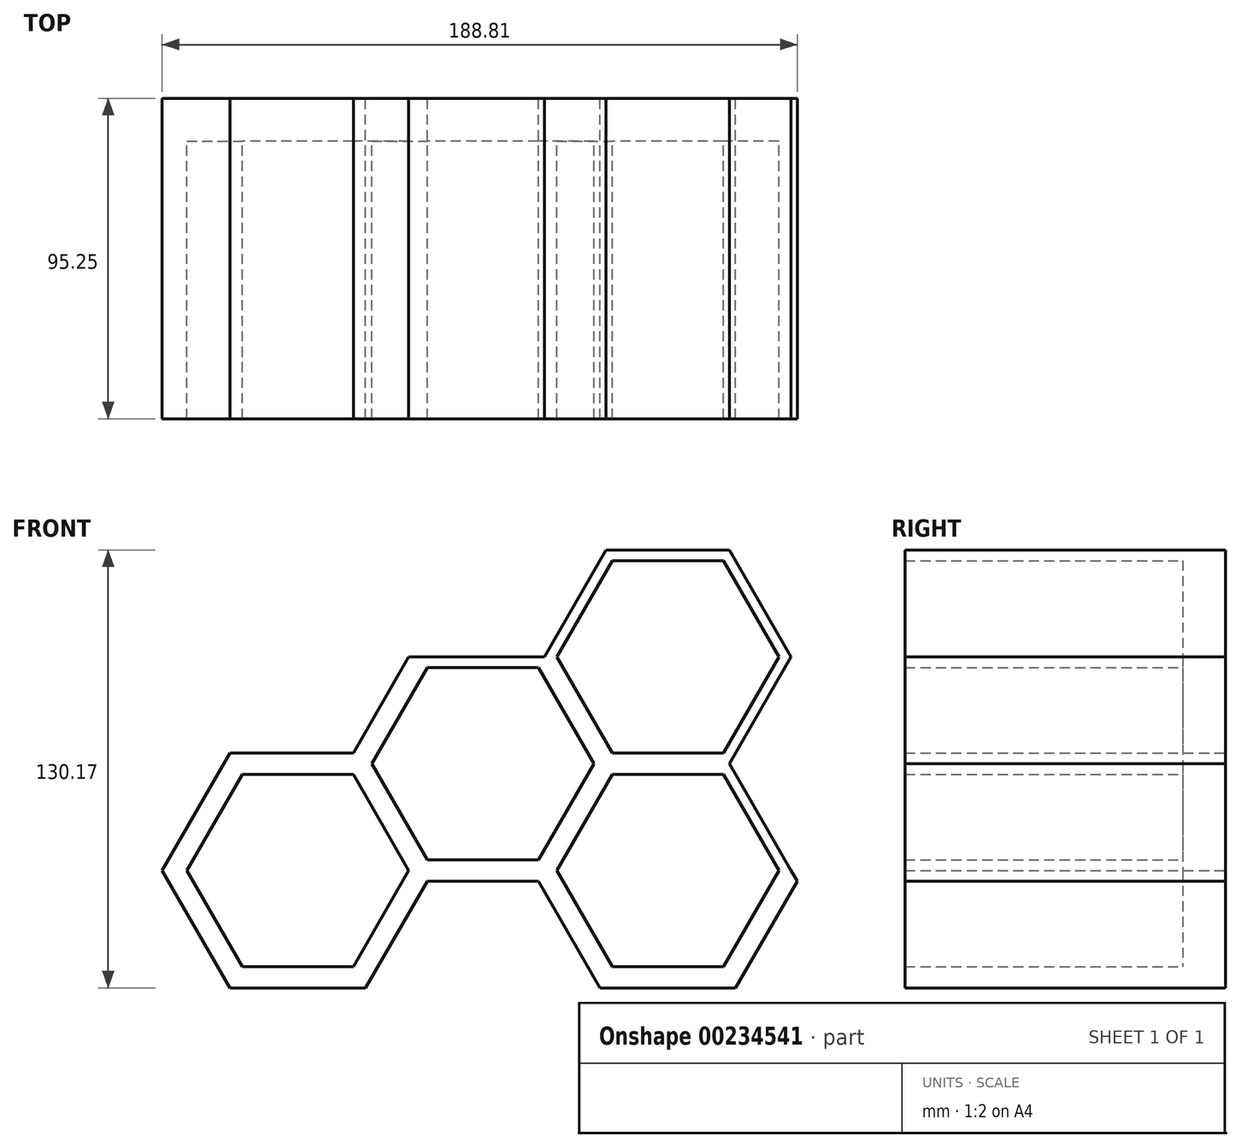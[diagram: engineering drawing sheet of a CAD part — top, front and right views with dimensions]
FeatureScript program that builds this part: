
annotation { "Feature Type Name" : "Feature", "Feature Type Description" : "" }
export const myFeature = defineFeature(function(context is Context, id is Id, definition is map)
    precondition{}
    {
        {
            var Q0;
            Q0=qCreatedBy(makeId("Front.planeOp"),FACE);
            var sketch = newSketch(context, id + "F0", { "sketchPlane" : qUnion([Q0])});
            skLineSegment(sketch, "E0.5", {"start": v(-59.27, 3.3) * mm, "end": v(-77.6, 35.04) * mm});
            skCircle(sketch, "E1.cCircle", {"center": v(-95.93, 3.3) * mm, "radius": 28.58 * mm, "construction": true});
            skLineSegment(sketch, "E1.0", {"start": v(-128.93, 3.3) * mm, "end": v(-112.43, 31.87) * mm});
            skLineSegment(sketch, "E1.1", {"start": v(-112.43, 31.87) * mm, "end": v(-79.43, 31.87) * mm});
            skLineSegment(sketch, "E1.2", {"start": v(-79.43, 31.87) * mm, "end": v(-62.94, 3.3) * mm});
            skLineSegment(sketch, "E1.3", {"start": v(-62.94, 3.3) * mm, "end": v(-79.43, -25.28) * mm});
            skLineSegment(sketch, "E1.4", {"start": v(-79.43, -25.28) * mm, "end": v(-112.43, -25.28) * mm});
            skLineSegment(sketch, "E1.5", {"start": v(-112.43, -25.28) * mm, "end": v(-128.93, 3.3) * mm});
            skPoint(sketch, "E1.0.midPoint", {"position": v(-120.68, 17.58) * mm});
            skCircle(sketch, "E2.cCircle", {"center": v(-95.93, 3.3) * mm, "radius": 31.75 * mm, "construction": true});
            skLineSegment(sketch, "E2.0", {"start": v(-132.6, 3.3) * mm, "end": v(-114.26, 35.04) * mm});
            skLineSegment(sketch, "E2.1", {"start": v(-114.26, 35.04) * mm, "end": v(-77.6, 35.04) * mm});
            skLineSegment(sketch, "E2.2", {"start": v(-77.6, 35.04) * mm, "end": v(-59.27, 3.3) * mm});
            skLineSegment(sketch, "E2.3", {"start": v(-59.27, 3.3) * mm, "end": v(-77.6, -28.46) * mm});
            skLineSegment(sketch, "E2.4", {"start": v(-77.6, -28.46) * mm, "end": v(-114.26, -28.46) * mm});
            skLineSegment(sketch, "E2.5", {"start": v(-114.26, -28.46) * mm, "end": v(-132.6, 3.3) * mm});
            skPoint(sketch, "E2.0.midPoint", {"position": v(-123.43, 19.17) * mm});
            skLineSegment(sketch, "E3.3", {"start": v(-114.26, 35.04) * mm, "end": v(-132.6, 3.3) * mm});
            skLineSegment(sketch, "E3.4", {"start": v(-132.6, 3.3) * mm, "end": v(-169.26, 3.3) * mm});
            skLineSegment(sketch, "E4.4", {"start": v(-77.6, 35.04) * mm, "end": v(-114.26, 35.04) * mm});
            skLineSegment(sketch, "E5.0", {"start": v(-77.6, -28.46) * mm, "end": v(-59.27, 3.3) * mm});
            skLineSegment(sketch, "E5.5", {"start": v(-59.27, -60.2) * mm, "end": v(-77.6, -28.46) * mm});
            skPoint(sketch, "E5.0.midPoint", {"position": v(-68.44, -12.58) * mm});
            skCircle(sketch, "E6.cCircle", {"center": v(-150.93, -28.46) * mm, "radius": 28.58 * mm, "construction": true});
            skLineSegment(sketch, "E6.0", {"start": v(-183.92, -28.46) * mm, "end": v(-167.42, 0.12) * mm});
            skLineSegment(sketch, "E6.1", {"start": v(-167.42, 0.12) * mm, "end": v(-134.43, 0.12) * mm});
            skLineSegment(sketch, "E6.2", {"start": v(-134.43, 0.12) * mm, "end": v(-117.93, -28.46) * mm});
            skLineSegment(sketch, "E6.3", {"start": v(-117.93, -28.46) * mm, "end": v(-134.43, -57.03) * mm});
            skLineSegment(sketch, "E6.4", {"start": v(-134.43, -57.03) * mm, "end": v(-167.42, -57.03) * mm});
            skLineSegment(sketch, "E6.5", {"start": v(-167.42, -57.03) * mm, "end": v(-183.92, -28.46) * mm});
            skPoint(sketch, "E6.0.midPoint", {"position": v(-175.67, -14.17) * mm});
            skCircle(sketch, "E7.cCircle", {"center": v(-150.93, -28.46) * mm, "radius": 31.75 * mm, "construction": true});
            skLineSegment(sketch, "E7.0", {"start": v(-187.59, -28.46) * mm, "end": v(-169.26, 3.3) * mm});
            skLineSegment(sketch, "E7.1", {"start": v(-169.26, 3.3) * mm, "end": v(-132.6, 3.3) * mm});
            skLineSegment(sketch, "E7.2", {"start": v(-132.6, 3.3) * mm, "end": v(-114.26, -28.46) * mm});
            skLineSegment(sketch, "E7.3", {"start": v(-114.26, -28.46) * mm, "end": v(-132.6, -60.2) * mm});
            skLineSegment(sketch, "E7.4", {"start": v(-132.6, -60.2) * mm, "end": v(-169.26, -60.2) * mm});
            skLineSegment(sketch, "E7.5", {"start": v(-169.26, -60.2) * mm, "end": v(-187.59, -28.46) * mm});
            skCircle(sketch, "E8.cCircle", {"center": v(-95.93, -60.2) * mm, "radius": 28.57 * mm, "construction": true});
            skLineSegment(sketch, "E8.0", {"start": v(-128.93, -60.2) * mm, "end": v(-112.43, -31.63) * mm});
            skLineSegment(sketch, "E8.1", {"start": v(-112.43, -31.63) * mm, "end": v(-79.43, -31.63) * mm});
            skLineSegment(sketch, "E8.2", {"start": v(-79.43, -31.63) * mm, "end": v(-62.94, -60.2) * mm});
            skLineSegment(sketch, "E8.3", {"start": v(-62.94, -60.2) * mm, "end": v(-79.43, -88.78) * mm});
            skLineSegment(sketch, "E8.4", {"start": v(-79.43, -88.78) * mm, "end": v(-112.43, -88.78) * mm});
            skLineSegment(sketch, "E8.5", {"start": v(-112.43, -88.78) * mm, "end": v(-128.93, -60.2) * mm});
            skPoint(sketch, "E8.0.midPoint", {"position": v(-120.68, -45.92) * mm});
            skCircle(sketch, "E9.cCircle", {"center": v(-95.93, -60.2) * mm, "radius": 31.75 * mm, "construction": true});
            skLineSegment(sketch, "E9.0", {"start": v(-132.6, -60.2) * mm, "end": v(-114.26, -28.46) * mm});
            skLineSegment(sketch, "E9.1", {"start": v(-114.26, -28.46) * mm, "end": v(-77.6, -28.46) * mm});
            skLineSegment(sketch, "E9.2", {"start": v(-77.6, -28.46) * mm, "end": v(-59.27, -60.2) * mm});
            skLineSegment(sketch, "E9.3", {"start": v(-59.27, -60.2) * mm, "end": v(-77.6, -91.96) * mm});
            skLineSegment(sketch, "E9.4", {"start": v(-77.6, -91.96) * mm, "end": v(-114.26, -91.96) * mm});
            skLineSegment(sketch, "E9.5", {"start": v(-114.26, -91.96) * mm, "end": v(-132.6, -60.2) * mm});
            skPoint(sketch, "E9.0.midPoint", {"position": v(-123.43, -44.33) * mm});
            skCircle(sketch, "E10.cCircle", {"center": v(-205.92, -60.2) * mm, "radius": 28.58 * mm, "construction": true});
            skLineSegment(sketch, "E10.0", {"start": v(-238.91, -60.2) * mm, "end": v(-222.42, -31.63) * mm});
            skLineSegment(sketch, "E10.1", {"start": v(-222.42, -31.63) * mm, "end": v(-189.42, -31.63) * mm});
            skLineSegment(sketch, "E10.2", {"start": v(-189.42, -31.63) * mm, "end": v(-172.92, -60.2) * mm});
            skLineSegment(sketch, "E10.3", {"start": v(-172.92, -60.2) * mm, "end": v(-189.42, -88.78) * mm});
            skLineSegment(sketch, "E10.4", {"start": v(-189.42, -88.78) * mm, "end": v(-222.42, -88.78) * mm});
            skLineSegment(sketch, "E10.5", {"start": v(-222.42, -88.78) * mm, "end": v(-238.91, -60.2) * mm});
            skPoint(sketch, "E10.0.midPoint", {"position": v(-230.66, -45.92) * mm});
            skCircle(sketch, "E11.cCircle", {"center": v(-205.92, -60.2) * mm, "radius": 31.75 * mm, "construction": true});
            skLineSegment(sketch, "E11.0", {"start": v(-242.58, -60.2) * mm, "end": v(-224.25, -28.46) * mm});
            skLineSegment(sketch, "E11.1", {"start": v(-224.25, -28.46) * mm, "end": v(-187.59, -28.46) * mm});
            skLineSegment(sketch, "E11.2", {"start": v(-187.59, -28.46) * mm, "end": v(-169.26, -60.2) * mm});
            skLineSegment(sketch, "E11.3", {"start": v(-169.26, -60.2) * mm, "end": v(-187.59, -91.96) * mm});
            skLineSegment(sketch, "E11.4", {"start": v(-187.59, -91.96) * mm, "end": v(-224.25, -91.96) * mm});
            skLineSegment(sketch, "E11.5", {"start": v(-224.25, -91.96) * mm, "end": v(-242.58, -60.2) * mm});
            skPoint(sketch, "E11.0.midPoint", {"position": v(-233.41, -44.33) * mm});
            skLineSegment(sketch, "E12", {"start": v(-172.92, 3.3) * mm, "end": v(-189.42, -25.28) * mm});
            skLineSegment(sketch, "E13", {"start": v(-189.42, -25.28) * mm, "end": v(-226.08, -25.28) * mm});
            skLineSegment(sketch, "E14", {"start": v(-226.08, -25.28) * mm, "end": v(-246.25, -60.2) * mm});
            skLineSegment(sketch, "E15", {"start": v(-246.25, -60.2) * mm, "end": v(-226.08, -95.13) * mm});
            skLineSegment(sketch, "E16", {"start": v(-226.08, -95.13) * mm, "end": v(-185.75, -95.13) * mm});
            skLineSegment(sketch, "E17", {"start": v(-185.75, -95.13) * mm, "end": v(-167.42, -63.38) * mm});
            skLineSegment(sketch, "E18", {"start": v(-167.42, -63.38) * mm, "end": v(-134.43, -63.38) * mm});
            skLineSegment(sketch, "E19", {"start": v(-134.43, -63.38) * mm, "end": v(-116.1, -95.13) * mm});
            skLineSegment(sketch, "E20", {"start": v(-116.1, -95.13) * mm, "end": v(-75.77, -95.13) * mm});
            skLineSegment(sketch, "E21", {"start": v(-75.77, -95.13) * mm, "end": v(-57.44, -63.38) * mm});
            skLineSegment(sketch, "E22", {"start": v(-172.92, 3.3) * mm, "end": v(-169.26, 3.3) * mm});
            skLineSegment(sketch, "E23", {"start": v(-57.44, -63.38) * mm, "end": v(-59.27, -60.2) * mm});
            skSolve(sketch);
        }
        {
            var Q0;
            Q0=makeQuery(id+"F0.imprint","IMPRINT",FACE,{"disambiguationData":[TD([[makeQuery(id+"F0.imprint","IMPRINT",EDGE,{"derivedFrom":sQuery(id+"F0.wireOp",EDGE,"68d16a58-0471-4e1c-b2b3-2a61df7c0d9d.0")}),-1.0]])]});
            var Q1;
            Q1=makeQuery(id+"F0.imprint","IMPRINT",FACE,{"disambiguationData":[TD([[makeQuery(id+"F0.imprint","IMPRINT",EDGE,{"derivedFrom":sQuery(id+"F0.wireOp",EDGE,"ae29455d-c252-400a-b569-c5a1c48e1351.0")}),-1.0]])]});
            var Q2;
            Q2=makeQuery(id+"F0.imprint","IMPRINT",FACE,{"disambiguationData":[TD([[makeQuery(id+"F0.imprint","IMPRINT",EDGE,{"derivedFrom":sQuery(id+"F0.wireOp",EDGE,"cad1e4f3-bd43-45ec-b31a-1d5006939c94.0")}),-1.0]])]});
            var Q3;
            Q3=makeQuery(id+"F0.imprint","IMPRINT",FACE,{"disambiguationData":[TD([[makeQuery(id+"F0.imprint","IMPRINT",EDGE,{"derivedFrom":sQuery(id+"F0.wireOp",EDGE,"E10.0")}),-1.0]])]});
            var Q4;
            Q4=makeQuery(id+"F0.imprint","IMPRINT",FACE,{"disambiguationData":[TD([[makeQuery(id+"F0.imprint","IMPRINT",EDGE,{"derivedFrom":sQuery(id+"F0.wireOp",EDGE,"8c75d941-d110-4871-aa41-90a72d60fb2b.0")}),-1.0]])]});
            var Q5;
            Q5=makeQuery(id+"F0.imprint","IMPRINT",FACE,{"disambiguationData":[TD([[makeQuery(id+"F0.imprint","IMPRINT",EDGE,{"derivedFrom":sQuery(id+"F0.wireOp",EDGE,"258573fa-3544-418e-8bc5-5d37e5b8ba09.0")}),-1.0]])]});
            var Q6;
            Q6=makeQuery(id+"F0.imprint","IMPRINT",FACE,{"disambiguationData":[TD([[makeQuery(id+"F0.imprint","IMPRINT",EDGE,{"derivedFrom":sQuery(id+"F0.wireOp",EDGE,"0bf0733b-7d93-4c2e-8366-56d2cde24658.0")}),-1.0]])]});
            var Q7;
            Q7=makeQuery(id+"F0.imprint","IMPRINT",FACE,{"disambiguationData":[TD([[makeQuery(id+"F0.imprint","IMPRINT",EDGE,{"derivedFrom":sQuery(id+"F0.wireOp",EDGE,"93717492-86db-456f-ae55-f71e4e93837b.0")}),-1.0]])]});
            var Q8;
            Q8=makeQuery(id+"F0.imprint","IMPRINT",FACE,{"disambiguationData":[TD([[makeQuery(id+"F0.imprint","IMPRINT",EDGE,{"derivedFrom":sQuery(id+"F0.wireOp",EDGE,"f16ea8c9-6b67-4651-8441-f7eb3c0ce7d7.0")}),-1.0]])]});
            var Q9;
            Q9=makeQuery(id+"F0.imprint","IMPRINT",FACE,{"disambiguationData":[TD([[makeQuery(id+"F0.imprint","IMPRINT",EDGE,{"derivedFrom":sQuery(id+"F0.wireOp",EDGE,"0306a0a6-7289-4661-a415-5fa5585f2cb5.0")}),-1.0]])]});
            var Q10;
            Q10=makeQuery(id+"F0.imprint","IMPRINT",FACE,{"disambiguationData":[TD([[makeQuery(id+"F0.imprint","IMPRINT",EDGE,{"derivedFrom":sQuery(id+"F0.wireOp",EDGE,"0a91a14e-ea0c-483f-91eb-c48bd73cb0e6.0")}),-1.0]])]});
            var Q11;
            Q11=makeQuery(id+"F0.imprint","IMPRINT",FACE,{"disambiguationData":[TD([[makeQuery(id+"F0.imprint","IMPRINT",EDGE,{"derivedFrom":sQuery(id+"F0.wireOp",EDGE,"E8.0")}),-1.0]])]});
            var Q12;
            Q12=makeQuery(id+"F0.imprint","IMPRINT",FACE,{"disambiguationData":[TD([[makeQuery(id+"F0.imprint","IMPRINT",EDGE,{"derivedFrom":sQuery(id+"F0.wireOp",EDGE,"E6.0")}),-1.0]])]});
            var Q13;
            Q13=makeQuery(id+"F0.imprint","IMPRINT",FACE,{"disambiguationData":[TD([[makeQuery(id+"F0.imprint","IMPRINT",EDGE,{"derivedFrom":sQuery(id+"F0.wireOp",EDGE,"084ca30c-4dc0-463f-bfd9-557787ed9a2f.0")}),-1.0]])]});
            var Q14;
            Q14=makeQuery(id+"F0.imprint","IMPRINT",FACE,{"disambiguationData":[TD([[makeQuery(id+"F0.imprint","IMPRINT",EDGE,{"derivedFrom":sQuery(id+"F0.wireOp",EDGE,"06c29831-6b25-410b-9247-4ee044b7735c.0")}),-1.0]])]});
            var Q15;
            Q15=makeQuery(id+"F0.imprint","IMPRINT",FACE,{"disambiguationData":[TD([[makeQuery(id+"F0.imprint","IMPRINT",EDGE,{"derivedFrom":sQuery(id+"F0.wireOp",EDGE,"b8eec94e-d97e-439b-aaac-63499233db4c.0")}),-1.0]])]});
            var Q16;
            Q16=makeQuery(id+"F0.imprint","IMPRINT",FACE,{"disambiguationData":[TD([[makeQuery(id+"F0.imprint","IMPRINT",EDGE,{"derivedFrom":sQuery(id+"F0.wireOp",EDGE,"2e929887-9bb9-4083-9cef-f9a6a24e8e46.0")}),-1.0]])]});
            var Q17;
            Q17=makeQuery(id+"F0.imprint","IMPRINT",FACE,{"disambiguationData":[TD([[makeQuery(id+"F0.imprint","IMPRINT",EDGE,{"derivedFrom":sQuery(id+"F0.wireOp",EDGE,"23671680-92ab-419e-a071-eb0943a5012b.0")}),-1.0]])]});
            var Q18;
            Q18=makeQuery(id+"F0.imprint","IMPRINT",FACE,{"disambiguationData":[TD([[makeQuery(id+"F0.imprint","IMPRINT",EDGE,{"derivedFrom":sQuery(id+"F0.wireOp",EDGE,"a1daa6ae-7864-4614-8fb9-3511dddc1266.0")}),-1.0]])]});
            var Q19;
            Q19=makeQuery(id+"F0.imprint","IMPRINT",FACE,{"disambiguationData":[TD([[makeQuery(id+"F0.imprint","IMPRINT",EDGE,{"derivedFrom":sQuery(id+"F0.wireOp",EDGE,"E1.0")}),-1.0]])]});
            var Q20;
            Q20=makeQuery(id+"F0.imprint","IMPRINT",FACE,{"disambiguationData":[TD([[makeQuery(id+"F0.imprint","IMPRINT",EDGE,{"derivedFrom":sQuery(id+"F0.wireOp",EDGE,"f2dd3995-374a-43c5-8725-4a87181dc8c5.0")}),-1.0]])]});
            var Q21;
            Q21=makeQuery(id+"F0.imprint","IMPRINT",FACE,{"disambiguationData":[TD([[makeQuery(id+"F0.imprint","IMPRINT",EDGE,{"derivedFrom":sQuery(id+"F0.wireOp",EDGE,"1f2aec04-a318-49b9-a42e-ea2fce35ed6c.0")}),-1.0]])]});
            var Q22;
            Q22=makeQuery(id+"F0.imprint","IMPRINT",FACE,{"disambiguationData":[TD([[makeQuery(id+"F0.imprint","IMPRINT",EDGE,{"derivedFrom":sQuery(id+"F0.wireOp",EDGE,"f97fdbdd-69fc-44f1-b8f7-f6a6a25558e6.0")}),-1.0]])]});
            var Q23;
            Q23=makeQuery(id+"F0.imprint","IMPRINT",FACE,{"disambiguationData":[TD([[makeQuery(id+"F0.imprint","IMPRINT",EDGE,{"derivedFrom":sQuery(id+"F0.wireOp",EDGE,"4e92e904-9607-490d-a429-b319c41500d9.0")}),-1.0]])]});
            var Q24;
            Q24=makeQuery(id+"F0.imprint","IMPRINT",FACE,{"disambiguationData":[TD([[makeQuery(id+"F0.imprint","IMPRINT",EDGE,{"derivedFrom":sQuery(id+"F0.wireOp",EDGE,"084ca30c-4dc0-463f-bfd9-557787ed9a2f.0")}),1.0]])]});
            var Q25;
            Q25=makeQuery(id+"F0.imprint","IMPRINT",FACE,{"disambiguationData":[TD([[makeQuery(id+"F0.imprint","IMPRINT",EDGE,{"derivedFrom":sQuery(id+"F0.wireOp",EDGE,"1f2aec04-a318-49b9-a42e-ea2fce35ed6c.0")}),1.0]])]});
            var Q26;
            Q26=makeQuery(id+"F0.imprint","IMPRINT",FACE,{"disambiguationData":[TD([[makeQuery(id+"F0.imprint","IMPRINT",EDGE,{"derivedFrom":sQuery(id+"F0.wireOp",EDGE,"23671680-92ab-419e-a071-eb0943a5012b.0")}),1.0]])]});
            var Q27;
            Q27=makeQuery(id+"F0.imprint","IMPRINT",FACE,{"disambiguationData":[TD([[makeQuery(id+"F0.imprint","IMPRINT",EDGE,{"derivedFrom":sQuery(id+"F0.wireOp",EDGE,"2e929887-9bb9-4083-9cef-f9a6a24e8e46.0")}),1.0]])]});
            var Q28;
            Q28=makeQuery(id+"F0.imprint","IMPRINT",FACE,{"disambiguationData":[TD([[makeQuery(id+"F0.imprint","IMPRINT",EDGE,{"derivedFrom":sQuery(id+"F0.wireOp",EDGE,"4e92e904-9607-490d-a429-b319c41500d9.0")}),1.0]])]});
            var Q29;
            Q29=makeQuery(id+"F0.imprint","IMPRINT",FACE,{"disambiguationData":[TD([[makeQuery(id+"F0.imprint","IMPRINT",EDGE,{"derivedFrom":sQuery(id+"F0.wireOp",EDGE,"E10.0")}),1.0]])]});
            var Q30;
            Q30=makeQuery(id+"F0.imprint","IMPRINT",FACE,{"disambiguationData":[TD([[makeQuery(id+"F0.imprint","IMPRINT",EDGE,{"derivedFrom":sQuery(id+"F0.wireOp",EDGE,"ae29455d-c252-400a-b569-c5a1c48e1351.0")}),1.0]])]});
            var Q31;
            Q31=makeQuery(id+"F0.imprint","IMPRINT",FACE,{"disambiguationData":[TD([[makeQuery(id+"F0.imprint","IMPRINT",EDGE,{"derivedFrom":sQuery(id+"F0.wireOp",EDGE,"0a91a14e-ea0c-483f-91eb-c48bd73cb0e6.0")}),1.0]])]});
            var Q32;
            Q32=makeQuery(id+"F0.imprint","IMPRINT",FACE,{"disambiguationData":[TD([[makeQuery(id+"F0.imprint","IMPRINT",EDGE,{"derivedFrom":sQuery(id+"F0.wireOp",EDGE,"258573fa-3544-418e-8bc5-5d37e5b8ba09.0")}),1.0]])]});
            var Q33;
            Q33=makeQuery(id+"F0.imprint","IMPRINT",FACE,{"disambiguationData":[TD([[makeQuery(id+"F0.imprint","IMPRINT",EDGE,{"derivedFrom":sQuery(id+"F0.wireOp",EDGE,"E8.0")}),1.0]])]});
            var Q34;
            Q34=makeQuery(id+"F0.imprint","IMPRINT",FACE,{"disambiguationData":[TD([[makeQuery(id+"F0.imprint","IMPRINT",EDGE,{"derivedFrom":sQuery(id+"F0.wireOp",EDGE,"f97fdbdd-69fc-44f1-b8f7-f6a6a25558e6.0")}),1.0]])]});
            var Q35;
            Q35=makeQuery(id+"F0.imprint","IMPRINT",FACE,{"disambiguationData":[TD([[makeQuery(id+"F0.imprint","IMPRINT",EDGE,{"derivedFrom":sQuery(id+"F0.wireOp",EDGE,"b8eec94e-d97e-439b-aaac-63499233db4c.0")}),1.0]])]});
            var Q36;
            Q36=makeQuery(id+"F0.imprint","IMPRINT",FACE,{"disambiguationData":[TD([[makeQuery(id+"F0.imprint","IMPRINT",EDGE,{"derivedFrom":sQuery(id+"F0.wireOp",EDGE,"8c75d941-d110-4871-aa41-90a72d60fb2b.0")}),1.0]])]});
            var Q37;
            Q37=makeQuery(id+"F0.imprint","IMPRINT",FACE,{"disambiguationData":[TD([[makeQuery(id+"F0.imprint","IMPRINT",EDGE,{"derivedFrom":sQuery(id+"F0.wireOp",EDGE,"f16ea8c9-6b67-4651-8441-f7eb3c0ce7d7.0")}),1.0]])]});
            var Q38;
            Q38=makeQuery(id+"F0.imprint","IMPRINT",FACE,{"disambiguationData":[TD([[makeQuery(id+"F0.imprint","IMPRINT",EDGE,{"derivedFrom":sQuery(id+"F0.wireOp",EDGE,"E1.0")}),1.0]])]});
            var Q39;
            Q39=makeQuery(id+"F0.imprint","IMPRINT",FACE,{"disambiguationData":[TD([[makeQuery(id+"F0.imprint","IMPRINT",EDGE,{"derivedFrom":sQuery(id+"F0.wireOp",EDGE,"68d16a58-0471-4e1c-b2b3-2a61df7c0d9d.0")}),1.0]])]});
            var Q40;
            Q40=makeQuery(id+"F0.imprint","IMPRINT",FACE,{"disambiguationData":[TD([[makeQuery(id+"F0.imprint","IMPRINT",EDGE,{"derivedFrom":sQuery(id+"F0.wireOp",EDGE,"0306a0a6-7289-4661-a415-5fa5585f2cb5.0")}),1.0]])]});
            var Q41;
            Q41=makeQuery(id+"F0.imprint","IMPRINT",FACE,{"disambiguationData":[TD([[makeQuery(id+"F0.imprint","IMPRINT",EDGE,{"derivedFrom":sQuery(id+"F0.wireOp",EDGE,"0bf0733b-7d93-4c2e-8366-56d2cde24658.0")}),1.0]])]});
            var Q42;
            Q42=makeQuery(id+"F0.imprint","IMPRINT",FACE,{"disambiguationData":[TD([[makeQuery(id+"F0.imprint","IMPRINT",EDGE,{"derivedFrom":sQuery(id+"F0.wireOp",EDGE,"06c29831-6b25-410b-9247-4ee044b7735c.0")}),1.0]])]});
            var Q43;
            Q43=makeQuery(id+"F0.imprint","IMPRINT",FACE,{"disambiguationData":[TD([[makeQuery(id+"F0.imprint","IMPRINT",EDGE,{"derivedFrom":sQuery(id+"F0.wireOp",EDGE,"E6.0")}),1.0]])]});
            var Q44;
            Q44=makeQuery(id+"F0.imprint","IMPRINT",FACE,{"disambiguationData":[TD([[makeQuery(id+"F0.imprint","IMPRINT",EDGE,{"derivedFrom":sQuery(id+"F0.wireOp",EDGE,"cad1e4f3-bd43-45ec-b31a-1d5006939c94.0")}),1.0]])]});
            var Q45;
            Q45=makeQuery(id+"F0.imprint","IMPRINT",FACE,{"disambiguationData":[TD([[makeQuery(id+"F0.imprint","IMPRINT",EDGE,{"derivedFrom":sQuery(id+"F0.wireOp",EDGE,"f2dd3995-374a-43c5-8725-4a87181dc8c5.0")}),1.0]])]});
            var Q46;
            Q46=makeQuery(id+"F0.imprint","IMPRINT",FACE,{"disambiguationData":[TD([[makeQuery(id+"F0.imprint","IMPRINT",EDGE,{"derivedFrom":sQuery(id+"F0.wireOp",EDGE,"a1daa6ae-7864-4614-8fb9-3511dddc1266.0")}),1.0]])]});
            var Q47;
            Q47=makeQuery(id+"F0.imprint","IMPRINT",FACE,{"disambiguationData":[TD([[makeQuery(id+"F0.imprint","IMPRINT",EDGE,{"derivedFrom":sQuery(id+"F0.wireOp",EDGE,"93717492-86db-456f-ae55-f71e4e93837b.0")}),1.0]])]});
            extrude(context, id + "F1", {"entities" : qUnion([Q0, Q1, Q2, Q3, Q4, Q5, Q6, Q7, Q8, Q9, Q10, Q11, Q12, Q13, Q14, Q15, Q16, Q17, Q18, Q19, Q20, Q21, Q22, Q23, Q24, Q25, Q26, Q27, Q28, Q29, Q30, Q31, Q32, Q33, Q34, Q35, Q36, Q37, Q38, Q39, Q40, Q41, Q42, Q43, Q44, Q45, Q46, Q47]), "depth" : 12.7 * mm});
        }
        {
            var Q0;
            Q0=makeQuery(id+"F0.imprint","IMPRINT",FACE,{"disambiguationData":[TD([[makeQuery(id+"F0.imprint","IMPRINT",EDGE,{"derivedFrom":sQuery(id+"F0.wireOp",EDGE,"8c75d941-d110-4871-aa41-90a72d60fb2b.0")}),1.0]])]});
            var Q1;
            Q1=makeQuery(id+"F0.imprint","IMPRINT",FACE,{"disambiguationData":[TD([[makeQuery(id+"F0.imprint","IMPRINT",EDGE,{"derivedFrom":sQuery(id+"F0.wireOp",EDGE,"b8eec94e-d97e-439b-aaac-63499233db4c.0")}),1.0]])]});
            var Q2;
            Q2=makeQuery(id+"F0.imprint","IMPRINT",FACE,{"disambiguationData":[TD([[makeQuery(id+"F0.imprint","IMPRINT",EDGE,{"derivedFrom":sQuery(id+"F0.wireOp",EDGE,"cad1e4f3-bd43-45ec-b31a-1d5006939c94.0")}),1.0]])]});
            var Q3;
            Q3=makeQuery(id+"F0.imprint","IMPRINT",FACE,{"disambiguationData":[TD([[makeQuery(id+"F0.imprint","IMPRINT",EDGE,{"derivedFrom":sQuery(id+"F0.wireOp",EDGE,"68d16a58-0471-4e1c-b2b3-2a61df7c0d9d.0")}),1.0]])]});
            var Q4;
            Q4=makeQuery(id+"F0.imprint","IMPRINT",FACE,{"disambiguationData":[TD([[makeQuery(id+"F0.imprint","IMPRINT",EDGE,{"derivedFrom":sQuery(id+"F0.wireOp",EDGE,"0306a0a6-7289-4661-a415-5fa5585f2cb5.0")}),1.0]])]});
            var Q5;
            Q5=makeQuery(id+"F0.imprint","IMPRINT",FACE,{"disambiguationData":[TD([[makeQuery(id+"F0.imprint","IMPRINT",EDGE,{"derivedFrom":sQuery(id+"F0.wireOp",EDGE,"084ca30c-4dc0-463f-bfd9-557787ed9a2f.0")}),1.0]])]});
            var Q6;
            Q6=makeQuery(id+"F0.imprint","IMPRINT",FACE,{"disambiguationData":[TD([[makeQuery(id+"F0.imprint","IMPRINT",EDGE,{"derivedFrom":sQuery(id+"F0.wireOp",EDGE,"4e92e904-9607-490d-a429-b319c41500d9.0")}),1.0]])]});
            var Q7;
            Q7=makeQuery(id+"F0.imprint","IMPRINT",FACE,{"disambiguationData":[TD([[makeQuery(id+"F0.imprint","IMPRINT",EDGE,{"derivedFrom":sQuery(id+"F0.wireOp",EDGE,"a1daa6ae-7864-4614-8fb9-3511dddc1266.0")}),1.0]])]});
            var Q8;
            Q8=makeQuery(id+"F0.imprint","IMPRINT",FACE,{"disambiguationData":[TD([[makeQuery(id+"F0.imprint","IMPRINT",EDGE,{"derivedFrom":sQuery(id+"F0.wireOp",EDGE,"93717492-86db-456f-ae55-f71e4e93837b.0")}),1.0]])]});
            var Q9;
            Q9=makeQuery(id+"F0.imprint","IMPRINT",FACE,{"disambiguationData":[TD([[makeQuery(id+"F0.imprint","IMPRINT",EDGE,{"derivedFrom":sQuery(id+"F0.wireOp",EDGE,"258573fa-3544-418e-8bc5-5d37e5b8ba09.0")}),1.0]])]});
            var Q10;
            Q10=makeQuery(id+"F0.imprint","IMPRINT",FACE,{"disambiguationData":[TD([[makeQuery(id+"F0.imprint","IMPRINT",EDGE,{"derivedFrom":sQuery(id+"F0.wireOp",EDGE,"f2dd3995-374a-43c5-8725-4a87181dc8c5.0")}),1.0]])]});
            var Q11;
            Q11=makeQuery(id+"F0.imprint","IMPRINT",FACE,{"disambiguationData":[TD([[makeQuery(id+"F0.imprint","IMPRINT",EDGE,{"derivedFrom":sQuery(id+"F0.wireOp",EDGE,"23671680-92ab-419e-a071-eb0943a5012b.0")}),1.0]])]});
            var Q12;
            Q12=makeQuery(id+"F0.imprint","IMPRINT",FACE,{"disambiguationData":[TD([[makeQuery(id+"F0.imprint","IMPRINT",EDGE,{"derivedFrom":sQuery(id+"F0.wireOp",EDGE,"06c29831-6b25-410b-9247-4ee044b7735c.0")}),1.0]])]});
            var Q13;
            Q13=makeQuery(id+"F0.imprint","IMPRINT",FACE,{"disambiguationData":[TD([[makeQuery(id+"F0.imprint","IMPRINT",EDGE,{"derivedFrom":sQuery(id+"F0.wireOp",EDGE,"ae29455d-c252-400a-b569-c5a1c48e1351.0")}),1.0]])]});
            var Q14;
            Q14=makeQuery(id+"F0.imprint","IMPRINT",FACE,{"disambiguationData":[TD([[makeQuery(id+"F0.imprint","IMPRINT",EDGE,{"derivedFrom":sQuery(id+"F0.wireOp",EDGE,"f97fdbdd-69fc-44f1-b8f7-f6a6a25558e6.0")}),1.0]])]});
            var Q15;
            Q15=makeQuery(id+"F0.imprint","IMPRINT",FACE,{"disambiguationData":[TD([[makeQuery(id+"F0.imprint","IMPRINT",EDGE,{"derivedFrom":sQuery(id+"F0.wireOp",EDGE,"2e929887-9bb9-4083-9cef-f9a6a24e8e46.0")}),1.0]])]});
            var Q16;
            Q16=makeQuery(id+"F0.imprint","IMPRINT",FACE,{"disambiguationData":[TD([[makeQuery(id+"F0.imprint","IMPRINT",EDGE,{"derivedFrom":sQuery(id+"F0.wireOp",EDGE,"0a91a14e-ea0c-483f-91eb-c48bd73cb0e6.0")}),1.0]])]});
            var Q17;
            Q17=makeQuery(id+"F0.imprint","IMPRINT",FACE,{"disambiguationData":[TD([[makeQuery(id+"F0.imprint","IMPRINT",EDGE,{"derivedFrom":sQuery(id+"F0.wireOp",EDGE,"E1.0")}),1.0]])]});
            var Q18;
            Q18=makeQuery(id+"F0.imprint","IMPRINT",FACE,{"disambiguationData":[TD([[makeQuery(id+"F0.imprint","IMPRINT",EDGE,{"derivedFrom":sQuery(id+"F0.wireOp",EDGE,"E8.0")}),1.0]])]});
            var Q19;
            Q19=makeQuery(id+"F0.imprint","IMPRINT",FACE,{"disambiguationData":[TD([[makeQuery(id+"F0.imprint","IMPRINT",EDGE,{"derivedFrom":sQuery(id+"F0.wireOp",EDGE,"E6.0")}),1.0]])]});
            var Q20;
            Q20=makeQuery(id+"F0.imprint","IMPRINT",FACE,{"disambiguationData":[TD([[makeQuery(id+"F0.imprint","IMPRINT",EDGE,{"derivedFrom":sQuery(id+"F0.wireOp",EDGE,"0bf0733b-7d93-4c2e-8366-56d2cde24658.0")}),1.0]])]});
            var Q21;
            Q21=makeQuery(id+"F0.imprint","IMPRINT",FACE,{"disambiguationData":[TD([[makeQuery(id+"F0.imprint","IMPRINT",EDGE,{"derivedFrom":sQuery(id+"F0.wireOp",EDGE,"E10.0")}),1.0]])]});
            var Q22;
            Q22=makeQuery(id+"F0.imprint","IMPRINT",FACE,{"disambiguationData":[TD([[makeQuery(id+"F0.imprint","IMPRINT",EDGE,{"derivedFrom":sQuery(id+"F0.wireOp",EDGE,"f16ea8c9-6b67-4651-8441-f7eb3c0ce7d7.0")}),1.0]])]});
            var Q23;
            Q23=makeQuery(id+"F0.imprint","IMPRINT",FACE,{"disambiguationData":[TD([[makeQuery(id+"F0.imprint","IMPRINT",EDGE,{"derivedFrom":sQuery(id+"F0.wireOp",EDGE,"1f2aec04-a318-49b9-a42e-ea2fce35ed6c.0")}),1.0]])]});
            var Q24;
            {var subQ6=sQuery(id+"F0.wireOp",EDGE,"E0.3");Q24=makeQuery(id+"F0.imprint","IMPRINT",FACE,{"disambiguationData":[TD([[makeQuery(id+"F0.imprint","IMPRINT",EDGE,{"derivedFrom":subQ6}),1.0]])]});}
            var Q25;
            Q25=makeQuery(id+"F0.imprint","IMPRINT",FACE,{"disambiguationData":[TD([[makeQuery(id+"F0.imprint","IMPRINT",EDGE,{"derivedFrom":sQuery(id+"F0.wireOp",EDGE,"E0.1")}),1.0]])]});
            var Q26;
            Q26=makeQuery(id+"F0.imprint","IMPRINT",FACE,{"disambiguationData":[TD([[makeQuery(id+"F0.imprint","IMPRINT",EDGE,{"derivedFrom":sQuery(id+"F0.wireOp",EDGE,"E7.0")}),1.0]])]});
            extrude(context, id + "F2", {"entities" : qUnion([Q0, Q1, Q2, Q3, Q4, Q5, Q6, Q7, Q8, Q9, Q10, Q11, Q12, Q13, Q14, Q15, Q16, Q17, Q18, Q19, Q20, Q21, Q22, Q23, Q24, Q25, Q26]), "operationType" : NewBodyOperationType.ADD, "depth" : 95.25 * mm});
        }
    });
